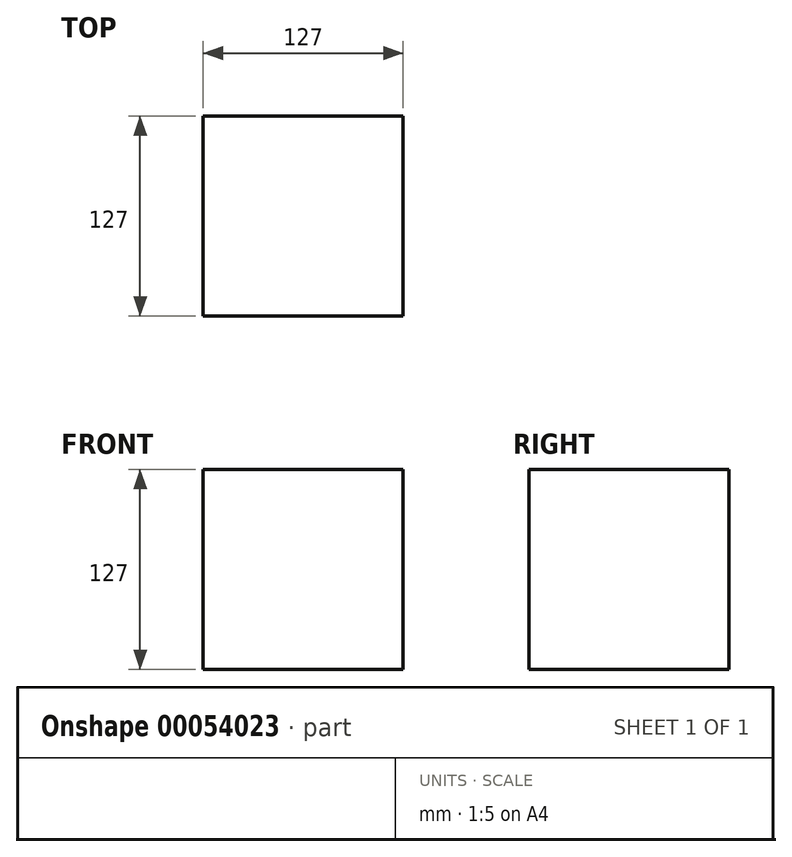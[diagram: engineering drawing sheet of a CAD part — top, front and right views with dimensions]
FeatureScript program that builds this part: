
annotation { "Feature Type Name" : "Feature", "Feature Type Description" : "" }
export const myFeature = defineFeature(function(context is Context, id is Id, definition is map)
    precondition{}
    {
        {
            var Q0;
            Q0=qCreatedBy(makeId("Top.planeOp"),FACE);
            var sketch = newSketch(context, id + "F0", { "sketchPlane" : qUnion([Q0])});
            skLineSegment(sketch, "E0", {"start": v(-83.68, 54.1) * mm, "end": v(-83.68, -72.9) * mm});
            skLineSegment(sketch, "E1", {"start": v(-83.68, -72.9) * mm, "end": v(43.32, -72.9) * mm});
            skLineSegment(sketch, "E2", {"start": v(43.32, -72.9) * mm, "end": v(43.32, 54.1) * mm});
            skLineSegment(sketch, "E3", {"start": v(43.32, 54.1) * mm, "end": v(-83.68, 54.1) * mm});
            skSolve(sketch);
        }
        {
            var Q0;
            Q0 = qSketchRegion(id + "F0", true);
            extrude(context, id + "F1", {"entities" : qUnion([Q0]), "depth" : 127 * mm});
        }
    });
